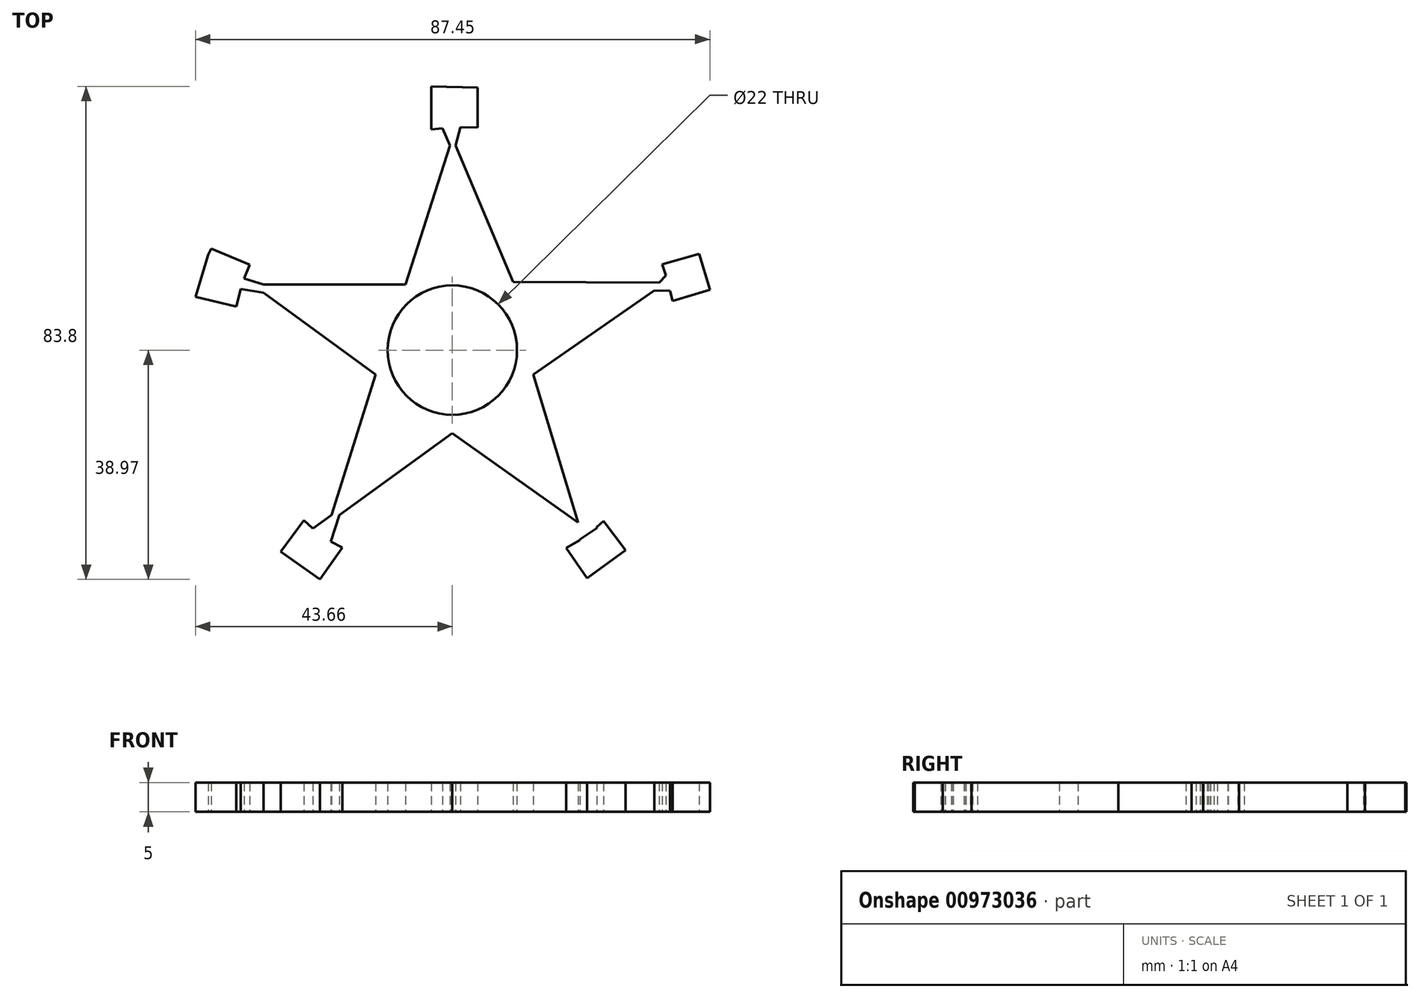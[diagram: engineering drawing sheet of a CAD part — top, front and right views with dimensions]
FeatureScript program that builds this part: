
annotation { "Feature Type Name" : "Feature", "Feature Type Description" : "" }
export const myFeature = defineFeature(function(context is Context, id is Id, definition is map)
    precondition{}
    {
        {
            var Q0;
            Q0=qCreatedBy(makeId("Top.planeOp"),FACE);
            var sketch = newSketch(context, id + "F0", { "sketchPlane" : qUnion([Q0])});
            skCircle(sketch, "E0", {"center": v(0, 0) * mm, "radius": 11 * mm});
            skLineSegment(sketch, "E1", {"start": v(-7.98, 11.15) * mm, "end": v(-33.98, 11.15) * mm});
            skLineSegment(sketch, "E2", {"start": v(-33.98, 11.15) * mm, "end": v(-13.01, -4.13) * mm});
            skLineSegment(sketch, "E3", {"start": v(-13.01, -4.13) * mm, "end": v(-20.92, -29.3) * mm});
            skLineSegment(sketch, "E4", {"start": v(-20.92, -29.3) * mm, "end": v(0, -14.14) * mm});
            skLineSegment(sketch, "E5", {"start": v(0, -14.14) * mm, "end": v(21.4, -29.3) * mm});
            skLineSegment(sketch, "E6", {"start": v(21.4, -29.3) * mm, "end": v(13.74, -4.13) * mm});
            skLineSegment(sketch, "E7", {"start": v(13.74, -4.13) * mm, "end": v(36.38, 11.5) * mm});
            skLineSegment(sketch, "E8", {"start": v(0, 36.11) * mm, "end": v(10.34, 11.57) * mm});
            skLineSegment(sketch, "E9", {"start": v(10.34, 11.57) * mm, "end": v(36.38, 11.5) * mm});
            skLineSegment(sketch, "E10", {"start": v(0, 36.11) * mm, "end": v(-7.98, 11.15) * mm});
            skLineSegment(sketch, "E11", {"start": v(-3.56, 37.51) * mm, "end": v(-3.56, 44.83) * mm});
            skLineSegment(sketch, "E12", {"start": v(4.32, 37.8) * mm, "end": v(4.32, 44.6) * mm});
            skLineSegment(sketch, "E13", {"start": v(37.47, 8.33) * mm, "end": v(43.79, 10.3) * mm});
            skLineSegment(sketch, "E14", {"start": v(35.66, 14.55) * mm, "end": v(41.96, 16.38) * mm});
            skLineSegment(sketch, "E15", {"start": v(25.68, -29.07) * mm, "end": v(29.46, -33.97) * mm});
            skLineSegment(sketch, "E16", {"start": v(19.33, -33.6) * mm, "end": v(22.9, -38.75) * mm});
            skLineSegment(sketch, "E17", {"start": v(-18.66, -33.56) * mm, "end": v(-22.5, -38.97) * mm});
            skLineSegment(sketch, "E18", {"start": v(-25.2, -28.93) * mm, "end": v(-29.16, -34.28) * mm});
            skLineSegment(sketch, "E19", {"start": v(-32.1, 11.15) * mm, "end": v(-35.36, 12.14) * mm});
            skLineSegment(sketch, "E20", {"start": v(-32.1, 9.77) * mm, "end": v(-35.98, 10.39) * mm});
            skLineSegment(sketch, "E21", {"start": v(0.56, 34.79) * mm, "end": v(1.38, 37.9) * mm});
            skLineSegment(sketch, "E22", {"start": v(-0.42, 34.79) * mm, "end": v(-1.64, 37.68) * mm});
            skLineSegment(sketch, "E23", {"start": v(35.18, 11.5) * mm, "end": v(36.3, 12.69) * mm});
            skLineSegment(sketch, "E24", {"start": v(34.37, 10.1) * mm, "end": v(37.03, 10.1) * mm});
            skLineSegment(sketch, "E25", {"start": v(20.6, -26.68) * mm, "end": v(24.58, -30.04) * mm});
            skLineSegment(sketch, "E26", {"start": v(19.68, -28.08) * mm, "end": v(21.69, -32.18) * mm});
            skLineSegment(sketch, "E27", {"start": v(-19.2, -28.05) * mm, "end": v(-20.62, -32.52) * mm});
            skLineSegment(sketch, "E28", {"start": v(-20.53, -28.05) * mm, "end": v(-23.7, -30.34) * mm});
            skLineSegment(sketch, "E29", {"start": v(-3.56, 44.83) * mm, "end": v(4.32, 44.6) * mm});
            skLineSegment(sketch, "E30", {"start": v(-3.56, 37.51) * mm, "end": v(-1.64, 37.68) * mm});
            skLineSegment(sketch, "E31", {"start": v(-1.64, 37.68) * mm, "end": v(1.38, 37.9) * mm});
            skLineSegment(sketch, "E32", {"start": v(1.38, 37.9) * mm, "end": v(4.32, 37.8) * mm});
            skLineSegment(sketch, "E33", {"start": v(-34.41, 14.5) * mm, "end": v(-35.36, 12.14) * mm});
            skLineSegment(sketch, "E34", {"start": v(-35.36, 12.14) * mm, "end": v(-35.98, 10.39) * mm});
            skLineSegment(sketch, "E35", {"start": v(-35.98, 10.39) * mm, "end": v(-36.72, 7.38) * mm});
            skLineSegment(sketch, "E36", {"start": v(35.66, 14.55) * mm, "end": v(36.3, 12.69) * mm});
            skLineSegment(sketch, "E37", {"start": v(36.3, 12.69) * mm, "end": v(36.38, 11.5) * mm});
            skLineSegment(sketch, "E38", {"start": v(36.38, 11.5) * mm, "end": v(37.03, 10.1) * mm});
            skLineSegment(sketch, "E39", {"start": v(37.47, 8.33) * mm, "end": v(37.03, 10.1) * mm});
            skLineSegment(sketch, "E40", {"start": v(41.96, 16.38) * mm, "end": v(43.79, 10.3) * mm});
            skLineSegment(sketch, "E41", {"start": v(25.68, -29.07) * mm, "end": v(24.58, -30.04) * mm});
            skLineSegment(sketch, "E42", {"start": v(24.54, -30.24) * mm, "end": v(21.69, -32.18) * mm});
            skLineSegment(sketch, "E43", {"start": v(21.72, -32.3) * mm, "end": v(19.33, -33.6) * mm});
            skLineSegment(sketch, "E44", {"start": v(22.9, -38.75) * mm, "end": v(29.46, -33.97) * mm});
            skLineSegment(sketch, "E45", {"start": v(-23.7, -30.34) * mm, "end": v(-25.2, -28.93) * mm});
            skLineSegment(sketch, "E46", {"start": v(-23.7, -30.34) * mm, "end": v(-20.62, -32.52) * mm});
            skLineSegment(sketch, "E47", {"start": v(-20.62, -32.52) * mm, "end": v(-18.66, -33.56) * mm});
            skLineSegment(sketch, "E48", {"start": v(-22.5, -38.97) * mm, "end": v(-29.16, -34.28) * mm});
            skLineSegment(sketch, "E49", {"start": v(-36.72, 7.38) * mm, "end": v(-43.66, 9.09) * mm});
            skLineSegment(sketch, "E50", {"start": v(-43.66, 9.09) * mm, "end": v(-41.5, 16.21) * mm});
            skLineSegment(sketch, "E51", {"start": v(-41.5, 16.21) * mm, "end": v(-40.97, 17.23) * mm});
            skLineSegment(sketch, "E52", {"start": v(-40.97, 17.23) * mm, "end": v(-34.41, 14.5) * mm});
            skLineSegment(sketch, "E53", {"start": v(24.58, -30.04) * mm, "end": v(24.54, -30.24) * mm});
            skLineSegment(sketch, "E54", {"start": v(21.69, -32.18) * mm, "end": v(21.72, -32.3) * mm});
            skSolve(sketch);
        }
        {
            var Q0;
            Q0=makeQuery(id+"F0.imprint","IMPRINT",FACE,{"disambiguationData":[TD([[makeQuery(id+"F0.imprint","IMPRINT",EDGE,{"derivedFrom":sQuery(id+"F0.wireOp",EDGE,"E33")}),-1.0]])]});
            var Q1;
            Q1=makeQuery(id+"F0.imprint","IMPRINT",FACE,{"disambiguationData":[TD([[makeQuery(id+"F0.imprint","IMPRINT",EDGE,{"derivedFrom":sQuery(id+"F0.wireOp",EDGE,"E0")}),-1.0]])]});
            var Q2;
            Q2=makeQuery(id+"F0.imprint","IMPRINT",FACE,{"disambiguationData":[TD([[makeQuery(id+"F0.imprint","IMPRINT",EDGE,{"derivedFrom":sQuery(id+"F0.wireOp",EDGE,"E13")}),1.0]])]});
            var Q3;
            {var subQ2=sQuery(id+"F0.wireOp",EDGE,"E24");Q3=makeQuery(id+"F0.imprint","IMPRINT",FACE,{"disambiguationData":[TD([[makeQuery(id+"F0.imprint","IMPRINT",EDGE,{"derivedFrom":subQ2}),1.0]])]});}
            var Q4;
            {var subQ2=sQuery(id+"F0.wireOp",EDGE,"E23");Q4=makeQuery(id+"F0.imprint","IMPRINT",FACE,{"disambiguationData":[TD([[makeQuery(id+"F0.imprint","IMPRINT",EDGE,{"derivedFrom":subQ2}),-1.0]])]});}
            var Q5;
            {var subQ4=sQuery(id+"F0.wireOp",EDGE,"E19");Q5=makeQuery(id+"F0.imprint","IMPRINT",FACE,{"disambiguationData":[TD([[makeQuery(id+"F0.imprint","IMPRINT",EDGE,{"derivedFrom":subQ4}),1.0]])]});}
            var Q6;
            {var subQ0=sQuery(id+"F0.wireOp",EDGE,"E21");Q6=makeQuery(id+"F0.imprint","IMPRINT",FACE,{"disambiguationData":[TD([[makeQuery(id+"F0.imprint","IMPRINT",EDGE,{"derivedFrom":subQ0}),1.0]])]});}
            var Q7;
            Q7=makeQuery(id+"F0.imprint","IMPRINT",FACE,{"disambiguationData":[TD([[makeQuery(id+"F0.imprint","IMPRINT",EDGE,{"derivedFrom":sQuery(id+"F0.wireOp",EDGE,"E11")}),-1.0]])]});
            var Q8;
            Q8=makeQuery(id+"F0.imprint","IMPRINT",FACE,{"disambiguationData":[TD([[makeQuery(id+"F0.imprint","IMPRINT",EDGE,{"derivedFrom":sQuery(id+"F0.wireOp",EDGE,"E17")}),-1.0]])]});
            var Q9;
            {var subQ1=sQuery(id+"F0.wireOp",EDGE,"E27");Q9=makeQuery(id+"F0.imprint","IMPRINT",FACE,{"disambiguationData":[TD([[makeQuery(id+"F0.imprint","IMPRINT",EDGE,{"derivedFrom":subQ1}),-1.0]])]});}
            var Q10;
            Q10=makeQuery(id+"F0.imprint","IMPRINT",FACE,{"disambiguationData":[TD([[makeQuery(id+"F0.imprint","IMPRINT",EDGE,{"derivedFrom":sQuery(id+"F0.wireOp",EDGE,"E15")}),-1.0]])]});
            extrude(context, id + "F1", {"entities" : qUnion([Q0, Q1, Q2, Q3, Q4, Q5, Q6, Q7, Q8, Q9, Q10]), "depth" : 5 * mm, "offsetDistance" : 25.4 * mm});
        }
    });
